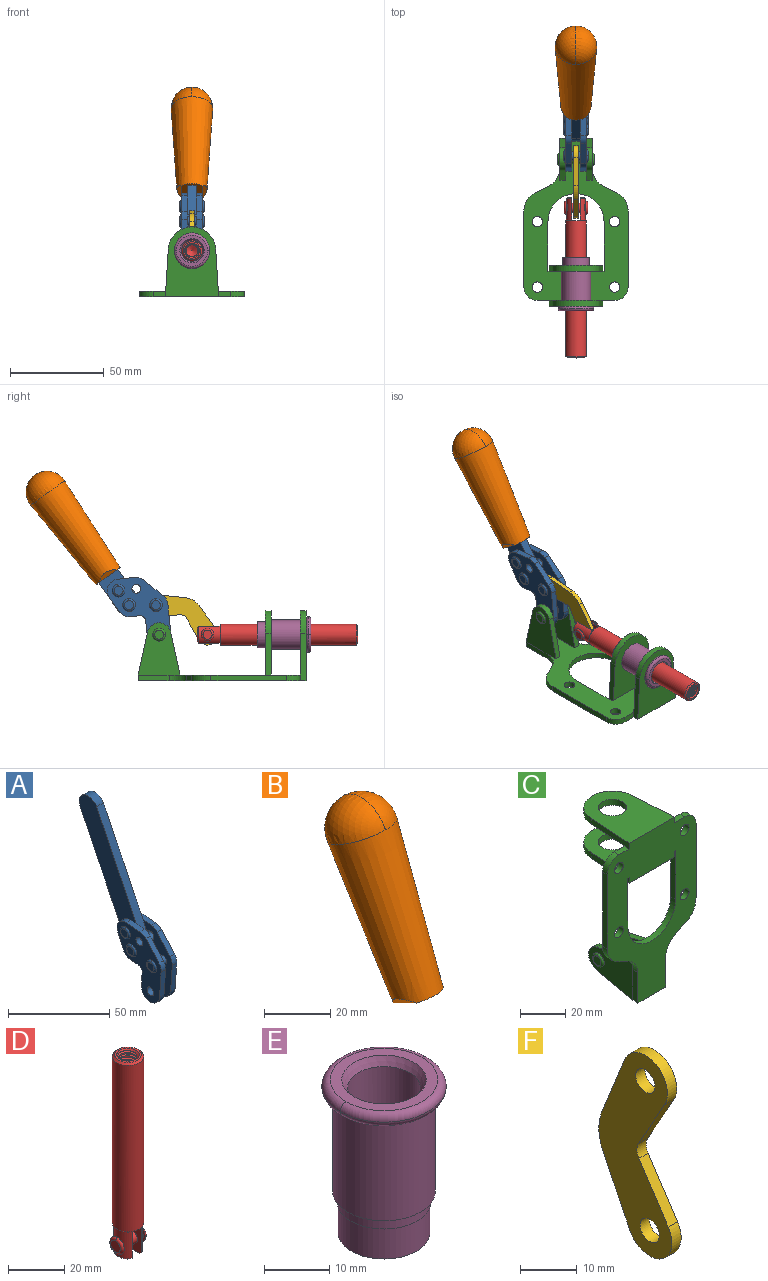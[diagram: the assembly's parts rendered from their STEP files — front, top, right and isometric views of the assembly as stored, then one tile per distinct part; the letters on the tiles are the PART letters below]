
ASSEMBLY  parts=6 mates=6
PART A: 59 faces, bbox 12.9x60.2x99.6 mm
  f0: torus R=2.39mm, axis (-1,0,0), area 14.9mm2, adj f20,f43,f51
  f1: torus R=2.39mm, axis (-1,0,0), area 14.9mm2, adj f19,f42,f51
  f2: torus R=2.39mm, axis (-1,0,0), area 14.9mm2, adj f18,f35,f51
  f3: torus R=2.39mm, axis (-1,0,0), area 14.9mm2, adj f14,f17,f23
  f4: torus R=2.39mm, axis (-1,0,0), area 14.9mm2, adj f13,f16,f23
  f5: torus R=2.39mm, axis (-1,0,0), area 14.9mm2, adj f12,f15,f23
  f6: cylinder r=2.39mm len=4.78mm, axis (1,0,0), area 46.5mm2, adj f48,f50,f51
  f7: cylinder r=2.39mm len=4.78mm, axis (1,0,0), area 46.5mm2, adj f50,f51
  f8: cylinder r=6.35mm len=12.68mm, axis (1,0,0), area 61.8mm2, adj f38,f39,f50,f51
  f9: cylinder r=2.39mm len=4.78mm, axis (-1,0,0), area 70.5mm2, adj f46,f50
  f10: cylinder r=2.39mm len=4.78mm, axis (-1,0,0), area 46.5mm2, adj f23,f45,f46
  f11: cylinder r=2.39mm len=4.78mm, axis (-1,0,0), area 46.5mm2, adj f23,f46
  f12: plane 4.78x4.78mm, normal (1,0,0), area 17.9mm2, adj f5,f15
  f13: plane 4.78x4.78mm, normal (1,0,0), area 17.9mm2, adj f4,f16
  f14: plane 4.78x4.78mm, normal (1,0,0), area 17.9mm2, adj f3,f17
  f15: torus R=2.39mm, axis (-1,0,0), area 14.9mm2, adj f5,f12,f23
  f16: torus R=2.39mm, axis (-1,0,0), area 14.9mm2, adj f4,f13,f23
  f17: torus R=2.39mm, axis (-1,0,0), area 14.9mm2, adj f3,f14,f23
  f18: plane 4.78x4.78mm, normal (-1,0,0), area 17.9mm2, adj f2,f35
  f19: plane 4.78x4.78mm, normal (-1,0,0), area 17.9mm2, adj f1,f42
  f20: plane 4.78x4.78mm, normal (-1,0,0), area 17.9mm2, adj f0,f43
  f21: plane 2.26x0.2mm, normal (1,0,0), area 0.2mm2, adj f31,f44
  f22: plane 2.26x0.2mm, normal (-1,0,0), area 0.2mm2, adj f41,f44
  f23: plane 39.37x30.77mm, normal (1,0,0), area 565.5mm2, adj f3,f4,f5,f10,f11,f15,f16,f17
  f24: cylinder r=6.1mm len=4.15mm, axis (-1,0,0), area 14.7mm2, adj f23,f25,f32,f46
  f25: plane 10.25x9.01mm, normal (0,-0.75,0.66), area 42.3mm2, adj f23,f24,f26,f46
  f26: cylinder r=6.35mm len=4.64mm, axis (-1,0,0), area 15.6mm2, adj f23,f25,f27,f46
  f27: plane 15.84x3.1mm, normal (0,-1,-0.07), area 49.2mm2, adj f23,f26,f28,f46
  f28: cylinder r=6.35mm len=12.68mm, axis (-1,0,0), area 61.8mm2, adj f23,f27,f29,f46
  f29: plane 8.11x3.1mm, normal (0,1,0.07), area 25.2mm2, adj f23,f28,f30,f46
  f30: cylinder r=3.05mm len=3.25mm, axis (-1,0,0), area 14.8mm2, adj f23,f29,f31,f46
  f31: plane 5.99x3.1mm, normal (0,0.07,-1), area 18.6mm2, adj f21,f23,f30,f44,f46
  f32: plane 9.5x3.1mm, normal (0,-0.07,1), area 29.5mm2, adj f23,f24,f33,f46,f47
  f33: cylinder r=6.1mm len=8.63mm, axis (-1,0,0), area 39.1mm2, adj f23,f32,f34,f47
  f34: plane 8.65x3.96mm, normal (0,0.91,-0.42), area 29.5mm2, adj f23,f33,f44,f47
  f35: torus R=2.39mm, axis (-1,0,0), area 14.9mm2, adj f2,f18,f51
  f36: plane 10.25x9.01mm, normal (0,-0.75,0.66), area 42.3mm2, adj f37,f49,f50,f51
  f37: cylinder r=6.35mm len=4.64mm, axis (1,0,0), area 15.6mm2, adj f36,f38,f50,f51
  f38: plane 15.84x3.1mm, normal (0,-1,-0.07), area 49.2mm2, adj f8,f37,f50,f51
  f39: plane 8.11x3.1mm, normal (0,1,0.07), area 25.2mm2, adj f8,f40,f50,f51
  f40: cylinder r=3.05mm len=3.25mm, axis (1,0,0), area 14.8mm2, adj f39,f41,f50,f51
  f41: plane 5.99x3.1mm, normal (0,0.07,-1), area 18.6mm2, adj f22,f40,f44,f50,f51
  f42: torus R=2.39mm, axis (-1,0,0), area 14.9mm2, adj f1,f19,f51
  f43: torus R=2.39mm, axis (-1,0,0), area 14.9mm2, adj f0,f20,f51
  f44: cylinder r=6.35mm len=12.12mm, axis (-1,0,0), area 128.9mm2, adj f21,f22,f23,f31,f34,f41,f46,f47
  f45: plane 2.65x1.35mm, normal (1,0,0), area 1mm2, adj f10,f55
  f46: plane 39.08x20.42mm, normal (-1,0,0), area 412.5mm2, adj f9,f10,f11,f24,f25,f26,f27,f28
  f47: plane 77.62x39.82mm, normal (1,0,0), area 850mm2, adj f32,f33,f34,f44,f53,f54,f55
  f48: plane 2.65x1.35mm, normal (-1,0,0), area 1mm2, adj f6,f55
  f49: cylinder r=6.1mm len=4.15mm, axis (1,0,0), area 14.7mm2, adj f36,f50,f51,f56
  f50: plane 39.08x20.42mm, normal (1,0,0), area 412.5mm2, adj f6,f7,f8,f9,f36,f37,f38,f39
  f51: plane 39.37x30.77mm, normal (-1,0,0), area 565.5mm2, adj f0,f1,f2,f6,f7,f8,f35,f36
  f52: plane 8.65x3.96mm, normal (0,0.91,-0.42), area 29.5mm2, adj f44,f51,f57,f58
  f53: plane 68.49x33.4mm, normal (0,0.9,-0.44), area 358.1mm2, adj f44,f47,f54,f58
  f54: cylinder r=6.35mm len=12.06mm, axis (1,0,0), area 93.7mm2, adj f47,f53,f55,f58
  f55: plane 68.49x33.4mm, normal (0,-0.9,0.44), area 358.1mm2, adj f44,f45,f46,f47,f48,f50,f54,f58
  f56: plane 9.5x3.1mm, normal (0,-0.07,1), area 29.5mm2, adj f49,f50,f51,f57,f58
  f57: cylinder r=6.1mm len=8.63mm, axis (1,0,0), area 39.1mm2, adj f51,f52,f56,f58
  f58: plane 77.62x39.82mm, normal (-1,0,0), area 850mm2, adj f44,f52,f53,f54,f55,f56,f57
PART B: 11 faces, bbox 22.3x42.6x64.5 mm
  f0: sphere r=11.13mm, area 411.4mm2, adj f1,f8
  f1: cone r=11.11mm half-angle=3.3deg, axis (0,0.44,0.9), area 3251.8mm2, adj f0,f7,f8,f9,f10
  f2: cylinder r=6.16mm len=11.7mm, axis (1,0,0), area 89.5mm2, adj f3,f4,f5,f6
  f3: plane 60.23x36.75mm, normal (-1,0,0), area 763.6mm2, adj f2,f4,f6,f10
  f4: plane 51.37x25.05mm, normal (0,0.9,-0.44), area 264.2mm2, adj f2,f3,f5,f10
  f5: plane 60.23x36.75mm, normal (1,0,0), area 763.6mm2, adj f2,f4,f6,f10
  f6: plane 51.37x25.05mm, normal (0,-0.9,0.44), area 264.2mm2, adj f2,f3,f5,f10
  f7: plane 9.95x5.95mm, normal (0.71,-0.31,-0.64), area 25.8mm2, adj f1,f10
  f8: sphere r=11.13mm, area 411.4mm2, adj f0,f1
  f9: plane 9.95x5.95mm, normal (-0.71,-0.31,-0.64), area 25.8mm2, adj f1,f10
  f10: plane 14.27x11.38mm, normal (0,-0.44,-0.9), area 106.7mm2, adj f1,f3,f4,f5,f6,f7,f9
PART C: 55 faces, bbox 55.7x37.4x89.8 mm
  f0: torus R=2.41mm, axis (-1,0,0), area 15mm2, adj f11,f15,f25
  f1: torus R=2.41mm, axis (-1,0,0), area 15mm2, adj f10,f12,f22
  f2: cylinder r=2.78mm len=5.56mm, axis (0,-1,0), area 54.2mm2, adj f30,f54
  f3: cylinder r=14.99mm len=29.97mm, axis (0,-1,0), area 145.9mm2, adj f30,f49,f53,f54
  f4: cylinder r=2.78mm len=5.56mm, axis (0,-1,0), area 54.2mm2, adj f30,f54
  f5: cylinder r=2.78mm len=5.56mm, axis (0,-1,0), area 54.2mm2, adj f30,f54
  f6: cylinder r=2.78mm len=5.56mm, axis (0,-1,0), area 54.2mm2, adj f30,f54
  f7: cylinder r=6.35mm len=12.7mm, axis (0,0,1), area 123.6mm2, adj f27,f51
  f8: cylinder r=6.35mm len=12.7mm, axis (0,0,-1), area 124.7mm2, adj f21,f35
  f9: cylinder r=2.41mm len=11.18mm, axis (-1,0,0), area 169.4mm2, adj f16,f19
  f10: plane 4.83x4.83mm, normal (1,0,0), area 18.3mm2, adj f1,f12
  f11: plane 4.83x4.83mm, normal (-1,0,0), area 18.3mm2, adj f0,f15
  f12: torus R=2.41mm, axis (-1,0,0), area 15mm2, adj f1,f10,f22
  f13: cylinder r=6.35mm len=12.41mm, axis (1,0,0), area 53.4mm2, adj f18,f19,f22,f23
  f14: cylinder r=6.35mm len=12.41mm, axis (-1,0,0), area 53.4mm2, adj f16,f17,f24,f25
  f15: torus R=2.41mm, axis (-1,0,0), area 15mm2, adj f0,f11,f25
  f16: plane 27.86x22.35mm, normal (1,0,0), area 425.4mm2, adj f9,f14,f17,f24,f30
  f17: plane 22.86x4.97mm, normal (0,0.21,0.98), area 72.5mm2, adj f14,f16,f25,f30
  f18: plane 22.86x4.97mm, normal (0,0.21,0.98), area 72.5mm2, adj f13,f19,f22,f30
  f19: plane 27.86x22.35mm, normal (-1,0,0), area 425.4mm2, adj f9,f13,f18,f23,f30
  f20: cylinder r=12.7mm len=25.35mm, axis (0,0,-1), area 119.8mm2, adj f21,f34,f35,f36
  f21: plane 34.21x28.07mm, normal (0,0,-1), area 702.4mm2, adj f8,f20,f30,f34,f36
  f22: plane 27.96x22.45mm, normal (1,0,0), area 407.2mm2, adj f1,f12,f13,f18,f23,f30,f42,f43
  f23: plane 22.86x4.97mm, normal (0,0.21,-0.98), area 72.5mm2, adj f13,f19,f22,f44
  f24: plane 22.86x4.97mm, normal (0,0.21,-0.98), area 72.5mm2, adj f14,f16,f25,f44
  f25: plane 27.86x22.35mm, normal (-1,0,0), area 407.1mm2, adj f0,f14,f15,f17,f24,f30,f45,f46
  f26: plane 3.1x0.95mm, normal (0,0,-1), area 2.7mm2, adj f30,f49,f50,f54
  f27: plane 34.21x28.07mm, normal (0,0,1), area 702.4mm2, adj f7,f28,f30,f50,f52
  f28: cylinder r=12.7mm len=25.35mm, axis (0,0,1), area 118.8mm2, adj f27,f50,f51,f52
  f29: plane 3.1x0.95mm, normal (0,0,-1), area 2.7mm2, adj f30,f52,f53,f54
  f30: plane 86.54x55.63mm, normal (0,1,0), area 2362.9mm2, adj f2,f3,f4,f5,f6,f16,f17,f18
  f31: plane 40.56x3.1mm, normal (-1,0,0), area 125.7mm2, adj f30,f32,f48,f54
  f32: cylinder r=7.11mm len=7.11mm, axis (0,-1,0), area 34.6mm2, adj f30,f31,f33,f54
  f33: plane 6.67x3.1mm, normal (0,0,1), area 20.4mm2, adj f30,f32,f34,f54
  f34: plane 25.39x3.13mm, normal (-1,0.06,0), area 79.5mm2, adj f20,f21,f33,f35,f54
  f35: plane 37.31x28.45mm, normal (0,0,1), area 789.9mm2, adj f8,f20,f34,f36,f54
  f36: plane 25.39x3.13mm, normal (1,0.06,0), area 79.5mm2, adj f20,f21,f35,f37,f54
  f37: plane 6.67x3.1mm, normal (0,0,1), area 20.4mm2, adj f30,f36,f38,f54
  f38: cylinder r=7.11mm len=7.11mm, axis (0,-1,0), area 34.6mm2, adj f30,f37,f39,f54
  f39: plane 40.56x3.1mm, normal (1,0,0), area 125.7mm2, adj f30,f38,f40,f54
  f40: cylinder r=11.18mm len=10.16mm, axis (0,-1,0), area 39.5mm2, adj f30,f39,f41,f54
  f41: plane 6.09x3.1mm, normal (0.42,0,-0.91), area 20.8mm2, adj f30,f40,f42,f54
  f42: cylinder r=11.18mm len=9.41mm, axis (0,-1,0), area 37.2mm2, adj f22,f30,f41,f43,f54
  f43: plane 16.5x3.1mm, normal (1,0,0), area 51.1mm2, adj f22,f42,f44,f54
  f44: plane 17.37x3.1mm, normal (0,0,-1), area 53.8mm2, adj f23,f24,f30,f43,f45,f54
  f45: plane 16.5x3.1mm, normal (-1,0,0), area 51.1mm2, adj f25,f44,f46,f54
  f46: cylinder r=11.18mm len=9.41mm, axis (0,-1,0), area 37.2mm2, adj f25,f30,f45,f47,f54
  f47: plane 6.09x3.1mm, normal (-0.42,0,-0.91), area 20.8mm2, adj f30,f46,f48,f54
  f48: cylinder r=11.18mm len=10.16mm, axis (0,-1,0), area 39.5mm2, adj f30,f31,f47,f54
  f49: plane 26.54x3.1mm, normal (-1,0,0), area 82.3mm2, adj f3,f26,f30,f54
  f50: plane 25.39x3.1mm, normal (1,0.06,0), area 78.8mm2, adj f26,f27,f28,f51,f54
  f51: plane 37.31x28.45mm, normal (0,0,-1), area 789.9mm2, adj f7,f28,f50,f52,f54
  f52: plane 25.39x3.1mm, normal (-1,0.06,0), area 78.8mm2, adj f27,f28,f29,f51,f54
  f53: plane 26.54x3.1mm, normal (1,0,0), area 82.3mm2, adj f3,f29,f30,f54
  f54: plane 89.66x55.63mm, normal (0,-1,0), area 2678.5mm2, adj f2,f3,f4,f5,f6,f26,f29,f31
PART D: 48 faces, bbox 12.6x11.1x86.1 mm
  f0: torus R=2.41mm, axis (-1,0,0), area 15mm2, adj f30,f32,f34
  f1: torus R=2.41mm, axis (-1,0,0), area 15mm2, adj f29,f31,f33
  f2: cylinder r=5.54mm len=72.39mm, axis (0,0,1), area 2518.5mm2, adj f3,f4,f42,f43
  f3: cone r=5.54mm half-angle=45deg, axis (0,0,1), area 7.6mm2, adj f2,f5,f41
  f4: cone r=5.54mm half-angle=45deg, axis (0,0,-1), area 34.9mm2, adj f2,f39
  f5: cylinder r=5.08mm len=11.48mm, axis (0,0,1), area 108.3mm2, adj f3,f7,f8,f41
  f6: cylinder r=2.41mm len=4.83mm, axis (-1,0,0), area 71.2mm2, adj f40,f41
  f7: cylinder r=2.41mm len=4.83mm, axis (-1,0,0), area 7.6mm2, adj f5,f34
  f8: cone r=5.08mm half-angle=45deg, axis (0,0,1), area 10.6mm2, adj f5,f37,f41
  f9: cone r=3.98mm half-angle=45deg, axis (0,0,1), area 17.6mm2, adj f27,f39,f45,f46,f47
  f10: cylinder r=2.41mm len=4.83mm, axis (-1,0,0), area 7.6mm2, adj f33,f38
  f11: cylinder r=3.2mm len=6.4mm, axis (0,0,1), area 78.4mm2, adj f12,f28,f44,f45,f47
  f12: cylinder r=3.2mm len=6.4mm, axis (0,0,1), area 10.5mm2, adj f11,f13,f45,f47
  f13: cylinder r=3.2mm len=6.4mm, axis (0,0,1), area 10.5mm2, adj f12,f14,f45,f47
  f14: cylinder r=3.2mm len=6.4mm, axis (0,0,1), area 10.5mm2, adj f13,f15,f45,f47
  f15: cylinder r=3.2mm len=6.4mm, axis (0,0,1), area 10.5mm2, adj f14,f16,f45,f47
  f16: cylinder r=3.2mm len=6.4mm, axis (0,0,1), area 10.5mm2, adj f15,f17,f45,f47
  f17: cylinder r=3.2mm len=6.4mm, axis (0,0,1), area 10.5mm2, adj f16,f18,f45,f47
  f18: cylinder r=3.2mm len=6.4mm, axis (0,0,1), area 10.5mm2, adj f17,f19,f45,f47
  f19: cylinder r=3.2mm len=6.4mm, axis (0,0,1), area 10.5mm2, adj f18,f20,f45,f47
  f20: cylinder r=3.2mm len=6.4mm, axis (0,0,1), area 10.5mm2, adj f19,f21,f45,f47
  f21: cylinder r=3.2mm len=6.4mm, axis (0,0,1), area 10.5mm2, adj f20,f22,f45,f47
  f22: cylinder r=3.2mm len=6.4mm, axis (0,0,1), area 10.5mm2, adj f21,f23,f45,f47
  f23: cylinder r=3.2mm len=6.4mm, axis (0,0,1), area 10.5mm2, adj f22,f24,f45,f47
  f24: cylinder r=3.2mm len=6.4mm, axis (0,0,1), area 10.5mm2, adj f23,f25,f45,f47
  f25: cylinder r=3.2mm len=6.4mm, axis (0,0,1), area 10.5mm2, adj f24,f26,f45,f47
  f26: cylinder r=3.2mm len=6.4mm, axis (0,0,1), area 10.5mm2, adj f25,f27,f45,f47
  f27: cylinder r=3.2mm len=6.4mm, axis (0,0,1), area 7.4mm2, adj f9,f26,f45,f47
  f28: cone r=3.2mm half-angle=60deg, axis (0,0,1), area 37.2mm2, adj f11
  f29: plane 4.83x4.83mm, normal (-1,0,0), area 18.3mm2, adj f1,f31
  f30: plane 4.83x4.83mm, normal (1,0,0), area 18.3mm2, adj f0,f32
  f31: torus R=2.41mm, axis (-1,0,0), area 15mm2, adj f1,f29,f33
  f32: torus R=2.41mm, axis (-1,0,0), area 15mm2, adj f0,f30,f34
  f33: plane 6.83x6.83mm, normal (1,0,0), area 18.3mm2, adj f1,f10,f31
  f34: plane 6.83x6.83mm, normal (-1,0,0), area 18.3mm2, adj f0,f7,f32
  f35: cone r=5.08mm half-angle=45deg, axis (0,0,1), area 10.6mm2, adj f36,f38,f40
  f36: plane 7.25x1.97mm, normal (0,0,-1), area 10mm2, adj f35,f40
  f37: plane 7.25x1.97mm, normal (0,0,-1), area 10mm2, adj f8,f41
  f38: cylinder r=5.08mm len=11.48mm, axis (0,0,1), area 108.3mm2, adj f10,f35,f40,f42
  f39: plane 9.55x9.55mm, normal (0,0,1), area 22mm2, adj f4,f9
  f40: plane 12.76x10.09mm, normal (1,0,0), area 95.7mm2, adj f6,f35,f36,f38,f42,f43
  f41: plane 12.76x10.09mm, normal (-1,0,0), area 95.7mm2, adj f3,f5,f6,f8,f37,f43
  f42: cone r=5.54mm half-angle=45deg, axis (0,0,1), area 7.6mm2, adj f2,f38,f40
  f43: plane 11.07x4.7mm, normal (0,0,-1), area 50.4mm2, adj f2,f40,f41
  f44: plane 0.89x0.62mm, normal (-1,0,0), area 0.3mm2, adj f11,f45,f46,f47
  f45: bspline ~24.8x7.63mm, area 266.6mm2, adj f9,f11,f12,f13,f14,f15,f16,f17
  f46: bspline ~24.87x7.63mm, area 73.6mm2, adj f9,f44,f45,f47
  f47: bspline ~24.98x7.63mm, area 272.5mm2, adj f9,f11,f12,f13,f14,f15,f16,f17
PART E: 15 faces, bbox 20.6x20.6x28.7 mm
  f0: torus R=8.26mm, axis (0,0,1), area 56.8mm2, adj f1,f10,f12
  f1: torus R=8.26mm, axis (0,0,1), area 56.8mm2, adj f0,f6,f13
  f2: cylinder r=5.59mm len=25.91mm, axis (0,0,1), area 909.6mm2, adj f3,f4
  f3: cone r=6.86mm half-angle=45deg, axis (0,0,-1), area 70.2mm2, adj f2,f14
  f4: cone r=6.47mm half-angle=30deg, axis (0,0,1), area 66.7mm2, adj f2,f13
  f5: cylinder r=7.04mm len=14.07mm, axis (0,0,1), area 252.6mm2, adj f11,f14
  f6: torus R=8.26mm, axis (0,0,1), area 56.8mm2, adj f1,f12,f13
  f7: cylinder r=7.16mm len=14.33mm, axis (0,0,1), area 91.5mm2, adj f9,f11
  f8: cylinder r=7.86mm len=18.42mm, axis (0,0,1), area 909.6mm2, adj f9,f10
  f9: plane 15.72x15.72mm, normal (0,0,-1), area 33mm2, adj f7,f8
  f10: plane 16.51x16.51mm, normal (0,0,-1), area 19.9mm2, adj f0,f8,f12
  f11: plane 14.33x14.33mm, normal (0,0,-1), area 5.7mm2, adj f5,f7
  f12: torus R=8.26mm, axis (0,0,1), area 56.8mm2, adj f0,f6,f10
  f13: plane 16.51x16.51mm, normal (0,0,1), area 82.7mm2, adj f1,f4,f6
  f14: plane 14.07x14.07mm, normal (0,0,-1), area 7.8mm2, adj f3,f5
PART F: 12 faces, bbox 2.3x18.2x42.8 mm
  f0: cylinder r=2.4mm len=4.8mm, axis (1,0,0), area 34.9mm2, adj f4,f11
  f1: cylinder r=10.41mm len=8.47mm, axis (1,0,0), area 20.2mm2, adj f4,f9,f10,f11
  f2: cylinder r=3.05mm len=3.16mm, axis (1,0,0), area 7.7mm2, adj f4,f6,f7,f11
  f3: cylinder r=2.4mm len=4.8mm, axis (1,0,0), area 34.9mm2, adj f4,f11
  f4: plane 42.81x18.23mm, normal (-1,0,0), area 414.1mm2, adj f0,f1,f2,f3,f5,f6,f7,f8
  f5: cylinder r=5.54mm len=10.67mm, axis (1,0,0), area 41.8mm2, adj f4,f6,f10,f11
  f6: plane 11.66x6.53mm, normal (0,-0.87,-0.49), area 30.9mm2, adj f2,f4,f5,f11
  f7: plane 11.17x7.33mm, normal (0,-0.84,0.55), area 30.9mm2, adj f2,f4,f8,f11
  f8: cylinder r=5.54mm len=10.51mm, axis (1,0,0), area 41.8mm2, adj f4,f7,f9,f11
  f9: plane 13.67x6.67mm, normal (0,0.9,-0.44), area 35.1mm2, adj f1,f4,f8,f11
  f10: plane 14.1x5.7mm, normal (0,0.93,0.37), area 35.1mm2, adj f1,f4,f5,f11
  f11: plane 42.81x18.23mm, normal (1,0,0), area 414.1mm2, adj f0,f1,f2,f3,f5,f6,f7,f8
PLACE A rot(axis=(-1,0,0),10deg) t=(0,14.66,60.49)mm
PLACE B rot(axis=(-1,0,0),10deg) t=(-0.04,14.66,60.49)mm
PLACE C rot(axis=(1,0,0),90deg) t=(0,1.23,0)mm fixed
PLACE D rot(axis=(1,0,0),90deg) t=(0,22.91,0)mm
PLACE E rot(axis=(1,0,0),90deg) t=(0,1.23,0)mm
PLACE F rot(axis=(1,0,0),121.8deg) t=(0,33.56,11.86)mm
MATE fastened C.f7 <-> E.f0  axis (0,-1,0) through (0,-45.16,24.61)mm
MATE revolute F.f5 <-> D.f6  axis (1,0,0) through (0,7.44,24.61)mm
MATE slider C.f7 <-> D.f2  axis (0,-1,0) through (0,-45.16,24.61)mm
MATE revolute A.f4 <-> F.f3  axis (-1,0,0) through (0,34.98,40.4)mm
MATE fastened A.f54 <-> B.f2  axis (-1,0,0) through (-2.35,94.13,102.1)mm
MATE revolute C.f0 <-> A.f7  axis (-1,0,0) through (0,33.32,24.61)mm
